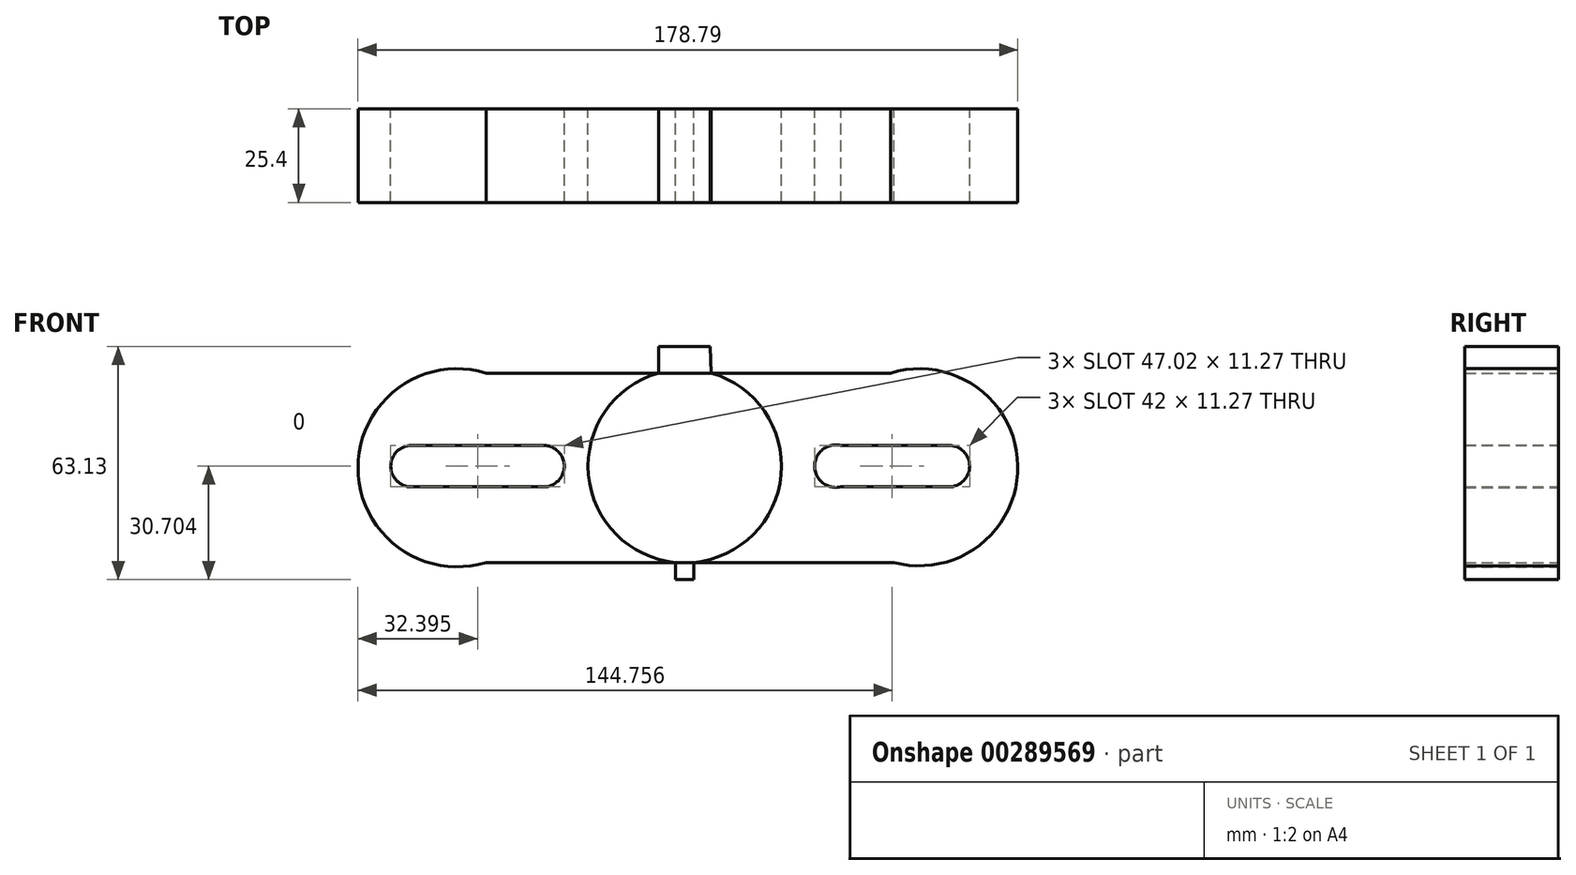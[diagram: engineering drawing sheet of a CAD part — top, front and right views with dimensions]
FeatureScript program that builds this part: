
annotation { "Feature Type Name" : "Feature", "Feature Type Description" : "" }
export const myFeature = defineFeature(function(context is Context, id is Id, definition is map)
    precondition{}
    {
        {
            var Q0;
            Q0=qCreatedBy(makeId("Front.planeOp"),FACE);
            var sketch = newSketch(context, id + "F0", { "sketchPlane" : qUnion([Q0])});
            skArc(sketch, "E0", {"start": v(-79.49, 30.85) * mm, "mid": v(-114.2, 5.2) * mm, "end": v(-79.49, -20.45) * mm});
            skLineSegment(sketch, "E1", {"start": v(-79.49, 30.85) * mm, "end": v(-32.77, 30.85) * mm});
            skPoint(sketch, "E2.end.orphan", {"position": v(31, -10.15) * mm});
            skArc(sketch, "E3", {"start": v(31, -20.45) * mm, "mid": v(64.59, 5.76) * mm, "end": v(30.14, 30.85) * mm});
            skLineSegment(sketch, "E4.bottom", {"start": v(16.62, 11.27) * mm, "end": v(45.92, 11.27) * mm});
            skLineSegment(sketch, "E4.top", {"start": v(16.62, 0) * mm, "end": v(45.92, 0) * mm});
            skArc(sketch, "E5", {"start": v(16.62, 11.27) * mm, "mid": v(9.56, 5.63) * mm, "end": v(16.62, 0) * mm});
            skLineSegment(sketch, "E6", {"start": v(-63.95, 11.27) * mm, "end": v(-99.73, 11.2) * mm});
            skLineSegment(sketch, "E7", {"start": v(-63.93, 0) * mm, "end": v(-99.71, 0) * mm});
            skArc(sketch, "E8", {"start": v(-99.73, 11.2) * mm, "mid": v(-105.31, 5.6) * mm, "end": v(-99.71, 0) * mm});
            skArc(sketch, "E9", {"start": v(-63.93, 0) * mm, "mid": v(-58.3, 5.64) * mm, "end": v(-63.95, 11.27) * mm});
            skArc(sketch, "E10", {"start": v(45.92, 0) * mm, "mid": v(51.56, 5.63) * mm, "end": v(45.92, 11.27) * mm});
            skLineSegment(sketch, "E11", {"start": v(-79.49, -20.45) * mm, "end": v(-28.12, -20.45) * mm});
            skArc(sketch, "E12", {"start": v(-23.15, -20.45) * mm, "mid": v(0.46, 3.27) * mm, "end": v(-18.5, 30.85) * mm});
            skLineSegment(sketch, "E13.trimOffspring", {"start": v(-18.5, 30.85) * mm, "end": v(30.14, 30.85) * mm});
            skArc(sketch, "E14.trimOffspring", {"start": v(-32.77, 30.85) * mm, "mid": v(-51.74, 3.27) * mm, "end": v(-28.12, -20.45) * mm});
            skLineSegment(sketch, "E15", {"start": v(-32.77, 30.85) * mm, "end": v(-18.5, 30.85) * mm});
            skLineSegment(sketch, "E16.trimOffspring", {"start": v(-23.15, -20.45) * mm, "end": v(31, -20.45) * mm});
            skLineSegment(sketch, "E17", {"start": v(-28.12, -20.45) * mm, "end": v(-23.15, -20.45) * mm});
            skLineSegment(sketch, "E18", {"start": v(-32.77, 30.85) * mm, "end": v(-32.79, 38.03) * mm});
            skLineSegment(sketch, "E19", {"start": v(-32.79, 38.03) * mm, "end": v(-18.73, 38.06) * mm});
            skLineSegment(sketch, "E20", {"start": v(-18.73, 38.06) * mm, "end": v(-18.5, 30.85) * mm});
            skLineSegment(sketch, "E21", {"start": v(-28.12, -20.45) * mm, "end": v(-28.12, -25.07) * mm});
            skLineSegment(sketch, "E22", {"start": v(-28.12, -25.07) * mm, "end": v(-23.15, -25.07) * mm});
            skLineSegment(sketch, "E23", {"start": v(-23.15, -25.07) * mm, "end": v(-23.15, -20.45) * mm});
            skSolve(sketch);
        }
        {
            var Q0;
            Q0=makeQuery(id+"F0.imprint","IMPRINT",FACE,{"disambiguationData":[TD([[makeQuery(id+"F0.imprint","IMPRINT",EDGE,{"derivedFrom":sQuery(id+"F0.wireOp",EDGE,"E0")}),1.0]])]});
            var Q1;
            Q1=makeQuery(id+"F0.imprint","IMPRINT",FACE,{"disambiguationData":[TD([[makeQuery(id+"F0.imprint","IMPRINT",EDGE,{"derivedFrom":sQuery(id+"F0.wireOp",EDGE,"E3")}),1.0]])]});
            var Q2;
            Q2=makeQuery(id+"F0.imprint","IMPRINT",FACE,{"disambiguationData":[TD([[makeQuery(id+"F0.imprint","IMPRINT",EDGE,{"derivedFrom":sQuery(id+"F0.wireOp",EDGE,"E15")}),1.0]])]});
            var Q3;
            Q3=makeQuery(id+"F0.imprint","IMPRINT",FACE,{"disambiguationData":[TD([[makeQuery(id+"F0.imprint","IMPRINT",EDGE,{"derivedFrom":sQuery(id+"F0.wireOp",EDGE,"E17")}),-1.0]])]});
            extrude(context, id + "F1", {"entities" : qUnion([Q0, Q1, Q2, Q3]), "depth" : 25.4 * mm});
        }
    });
